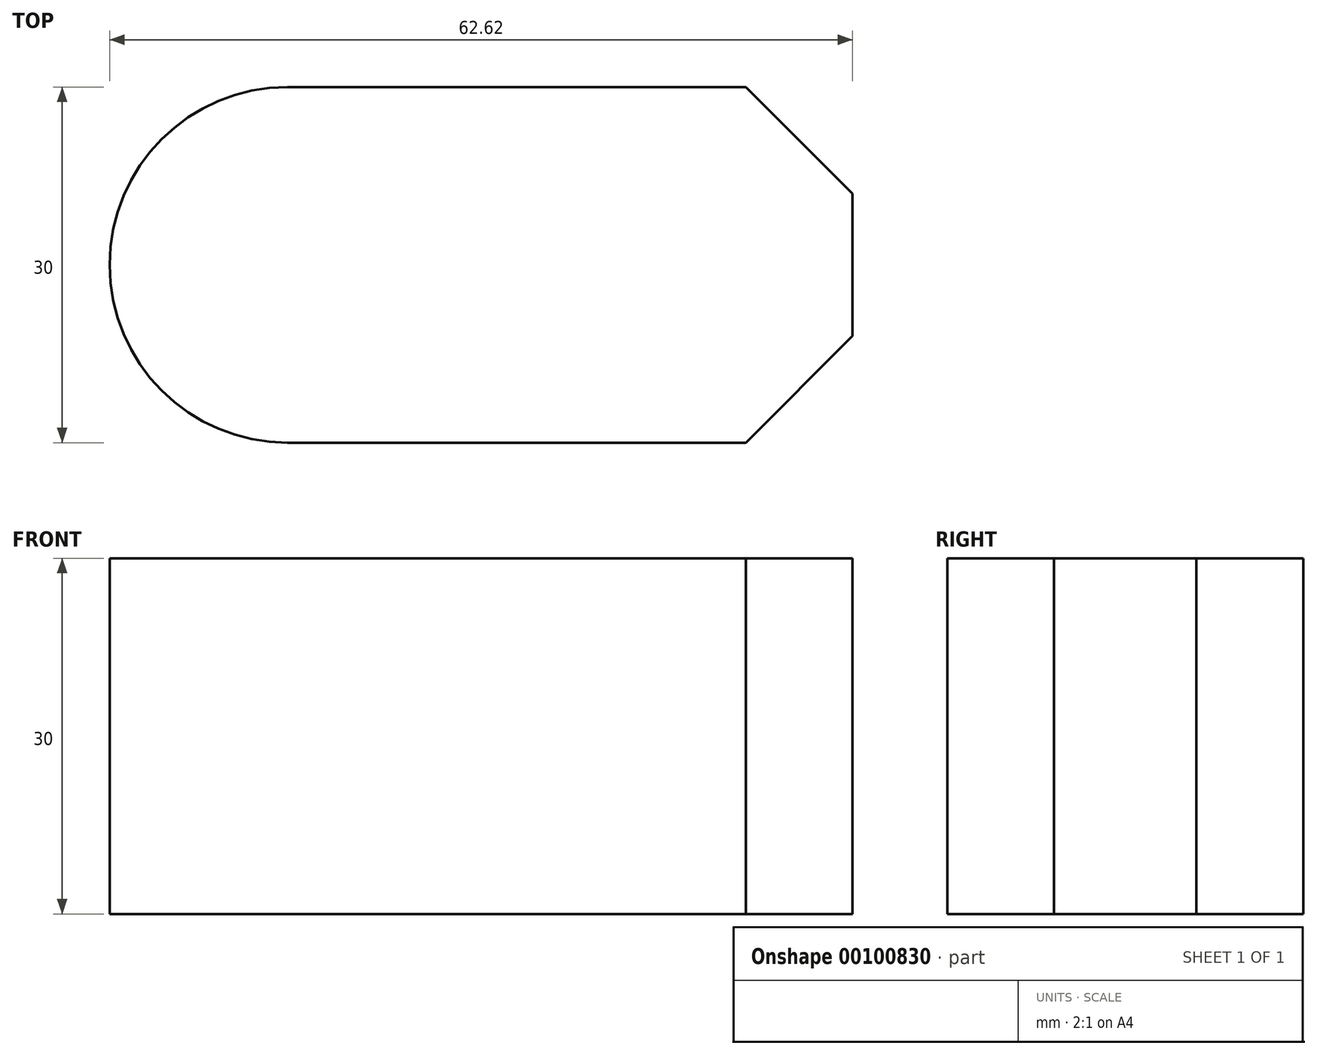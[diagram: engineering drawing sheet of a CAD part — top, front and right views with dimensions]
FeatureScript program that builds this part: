
annotation { "Feature Type Name" : "Feature", "Feature Type Description" : "" }
export const myFeature = defineFeature(function(context is Context, id is Id, definition is map)
    precondition{}
    {
        {
            var Q0;
            Q0=qCreatedBy(makeId("Top.planeOp"),FACE);
            var sketch = newSketch(context, id + "F0", { "sketchPlane" : qUnion([Q0])});
            skLineSegment(sketch, "E0.bottom", {"start": v(0, 0) * mm, "end": v(38.62, 0) * mm});
            skLineSegment(sketch, "E0.top", {"start": v(0, 30) * mm, "end": v(38.62, 30) * mm});
            skLineSegment(sketch, "E0.right", {"start": v(47.62, 9) * mm, "end": v(47.62, 21) * mm});
            skArc(sketch, "E1", {"start": v(0, 30) * mm, "mid": v(-15, 15) * mm, "end": v(0, 0) * mm});
            skLineSegment(sketch, "E2", {"start": v(38.62, 30) * mm, "end": v(47.62, 21) * mm});
            skLineSegment(sketch, "E3", {"start": v(38.62, 0) * mm, "end": v(47.62, 9) * mm});
            skSolve(sketch);
        }
        {
            var Q0;
            Q0 = qSketchRegion(id + "F0", true);
            extrude(context, id + "F1", {"entities" : qUnion([Q0]), "depth" : 30 * mm});
        }
    });
